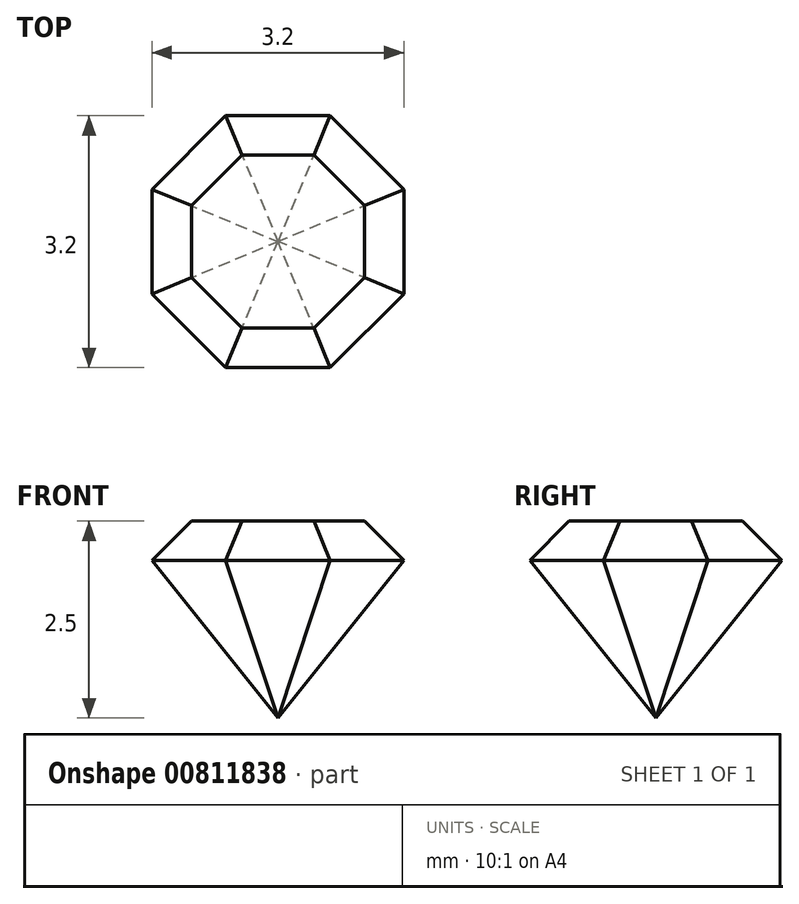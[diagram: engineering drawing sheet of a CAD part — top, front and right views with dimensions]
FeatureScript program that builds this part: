
annotation { "Feature Type Name" : "Feature", "Feature Type Description" : "" }
export const myFeature = defineFeature(function(context is Context, id is Id, definition is map)
    precondition{}
    {
        {
            var Q0;
            Q0=qCreatedBy(makeId("Top.planeOp"),FACE);
            var sketch = newSketch(context, id + "F0", { "sketchPlane" : qUnion([Q0])});
            skCircle(sketch, "E0.cCircle", {"center": v(0, 0) * mm, "radius": 1.6 * mm, "construction": true});
            skLineSegment(sketch, "E0.0", {"start": v(-1.6, -0.66) * mm, "end": v(-1.6, 0.66) * mm});
            skLineSegment(sketch, "E0.1", {"start": v(-1.6, 0.66) * mm, "end": v(-0.66, 1.6) * mm});
            skLineSegment(sketch, "E0.2", {"start": v(-0.66, 1.6) * mm, "end": v(0.66, 1.6) * mm});
            skLineSegment(sketch, "E0.3", {"start": v(0.66, 1.6) * mm, "end": v(1.6, 0.66) * mm});
            skLineSegment(sketch, "E0.4", {"start": v(1.6, 0.66) * mm, "end": v(1.6, -0.66) * mm});
            skLineSegment(sketch, "E0.5", {"start": v(1.6, -0.66) * mm, "end": v(0.66, -1.6) * mm});
            skLineSegment(sketch, "E0.6", {"start": v(0.66, -1.6) * mm, "end": v(-0.66, -1.6) * mm});
            skLineSegment(sketch, "E0.7", {"start": v(-0.66, -1.6) * mm, "end": v(-1.6, -0.66) * mm});
            skPoint(sketch, "E0.0.midPoint", {"position": v(-1.6, 0) * mm});
            skSolve(sketch);
        }
        {
            var Q0;
            Q0=makeQuery(id+"F0.imprint","IMPRINT",FACE,{"disambiguationData":[TD([[makeQuery(id+"F0.imprint","IMPRINT",EDGE,{"derivedFrom":sQuery(id+"F0.wireOp",EDGE,"E0.0")}),-1.0]])]});
            extrude(context, id + "F1", {"entities" : qUnion([Q0]), "depth" : .5 * mm, "offsetDistance" : 25 * mm});
        }
        {
            var Q0;
            Q0=makeQuery(id+"F1.opExtrude","CAP_FACE",FACE,{"disambiguationData":[OSD([sQuery(id+"F0.wireOp",EDGE,"E0.0"),sQuery(id+"F0.wireOp",EDGE,"E0.1"),sQuery(id+"F0.wireOp",EDGE,"E0.2"),sQuery(id+"F0.wireOp",EDGE,"E0.3"),sQuery(id+"F0.wireOp",EDGE,"E0.4"),sQuery(id+"F0.wireOp",EDGE,"E0.5"),sQuery(id+"F0.wireOp",EDGE,"E0.6"),sQuery(id+"F0.wireOp",EDGE,"E0.7")])],"isStart":false});
            chamfer(context, id + "F2", {"entities" : qUnion([Q0]), "chamferType" : ChamferType.OFFSET_ANGLE, "width" : .5 * mm, "oppositeDirection" : false, "angle" : 45 * degree, "tangentPropagation" : true});
        }
        {
            var Q0;
            Q0=qCreatedBy(makeId("Top.planeOp"),FACE);
            cPlane(context, id + "F3", {"entities" : qUnion([Q0]), "cplaneType" : CPlaneType.OFFSET, "offset" : 2 * mm, "oppositeDirection" : true, "width" : 150 * mm, "height" : 150 * mm});
        }
        {
            var Q0;
            Q0=qCreatedBy(id+"F3.planeOp",FACE);
            var sketch = newSketch(context, id + "F4", { "sketchPlane" : qUnion([Q0])});
            skPoint(sketch, "E1", {"position": v(0, 0) * mm});
            skSolve(sketch);
        }
        {
            var Q1;
            Q1=makeQuery(id+"F1.opExtrude","CAP_FACE",FACE,{"disambiguationData":[OSD([sQuery(id+"F0.wireOp",EDGE,"E0.0"),sQuery(id+"F0.wireOp",EDGE,"E0.1"),sQuery(id+"F0.wireOp",EDGE,"E0.2"),sQuery(id+"F0.wireOp",EDGE,"E0.3"),sQuery(id+"F0.wireOp",EDGE,"E0.4"),sQuery(id+"F0.wireOp",EDGE,"E0.5"),sQuery(id+"F0.wireOp",EDGE,"E0.6"),sQuery(id+"F0.wireOp",EDGE,"E0.7")])],"isStart":true});
            var Q2;
            Q2=sQuery(id+"F4.wireOp",VERTEX,"E1");
            loft(context, id + "F5", {"operationType" : NewBodyOperationType.ADD, "sheetProfilesArray" : [{ "sheetProfileEntities" : qUnion([Q1]) }, { "sheetProfileEntities" : qUnion([Q2]) }]});
        }
    });
